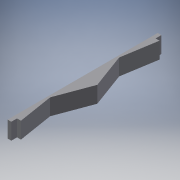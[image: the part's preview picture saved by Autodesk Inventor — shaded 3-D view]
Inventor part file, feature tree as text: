
AUTODESK INVENTOR PART (.ipt)
format: ipt  version: 2017 (Build 210142000, 142)  size: 121,344 bytes
history: native  units: in
note: dims shown in document units (in); Inventor stores cm internally (conversion verified against a paired STEP export)
features: extrude x3, sketch x3
ambient origin geometry x8: Origin, YZ Plane, XZ Plane, XY Plane, X Axis, Y Axis, Z Axis, Center Point
bodies: Solid1 (feature_tree)
feature tree (6):
  extrude  "Extrusion1"  Depth=0.134in
  sketch  "Sketch2"  dims[d2=0.134in d3=0.612in]
  extrude  "Extrusion2"  Depth=0.134in
  extrude  "Extrusion3"  Depth=0.065in
  sketch  "Sketch1"  dims[d0=2.436in d1=0.134in]
  sketch  "Sketch3"  dims[d4=1.223in d5=0.612in d6=0.035in d7=0.035in d8=0.2875in d9=0.0in d10=0.259in d12=0.065in d13=0.101in d14=0.0in d15=0.101in d16=0.0in d17=0.065in]
